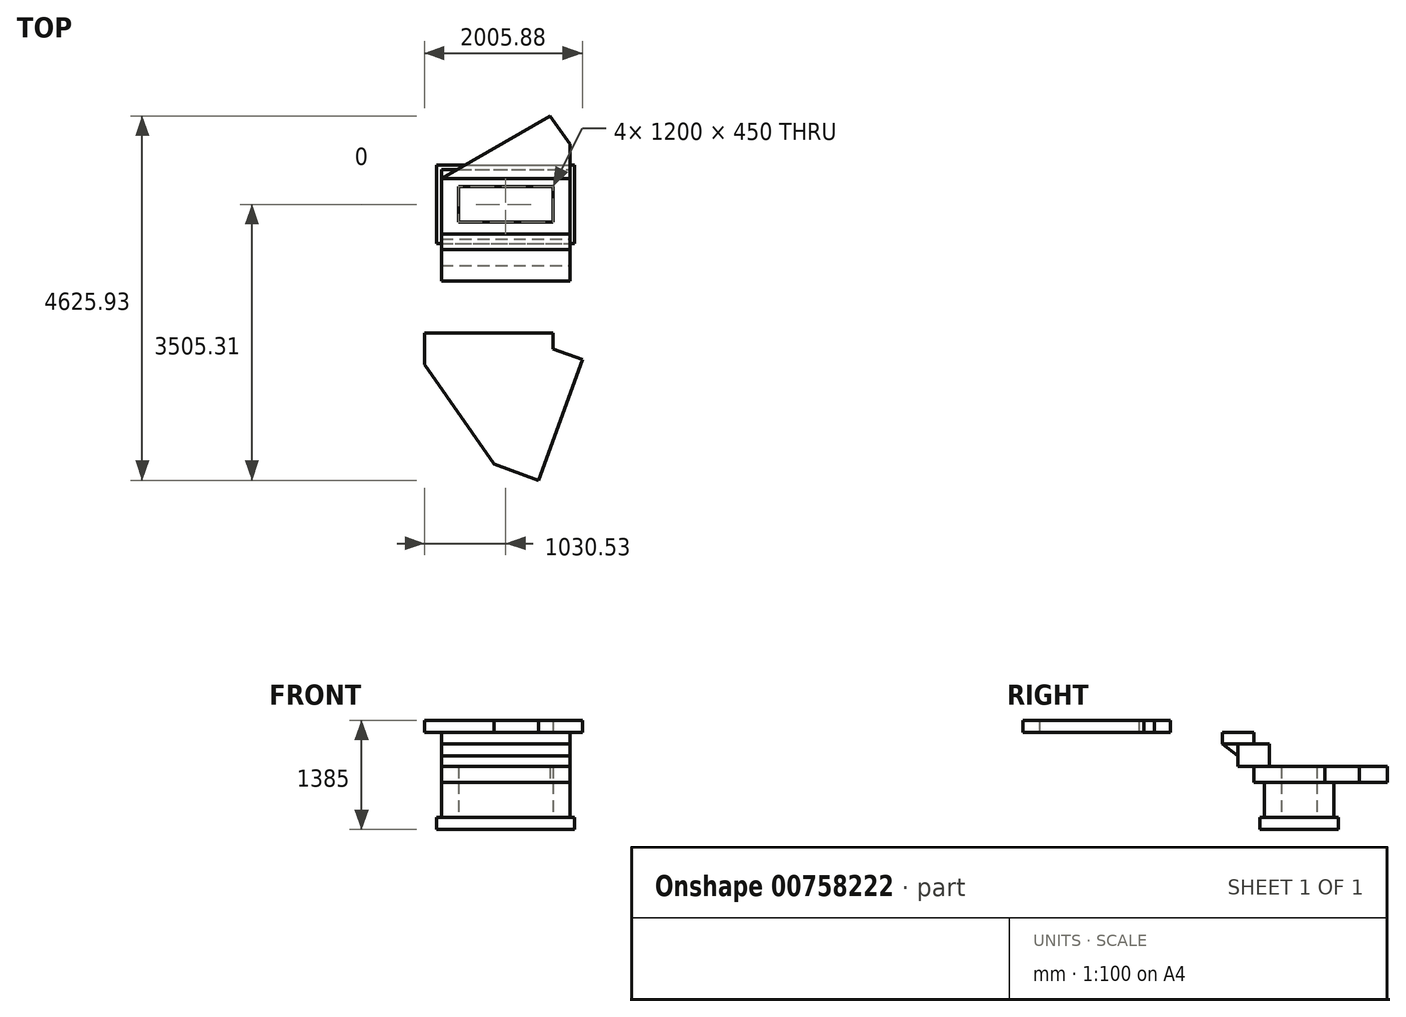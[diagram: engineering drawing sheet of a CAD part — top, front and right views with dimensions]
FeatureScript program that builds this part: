
annotation { "Feature Type Name" : "Feature", "Feature Type Description" : "" }
export const myFeature = defineFeature(function(context is Context, id is Id, definition is map)
    precondition{}
    {
        {
            var Q0;
            Q0=qCreatedBy(makeId("Top.planeOp"),FACE);
            var sketch = newSketch(context, id + "F0", { "sketchPlane" : qUnion([Q0])});
            skLineSegment(sketch, "E0", {"start": v(-102.22, -92.06) * mm, "end": v(-102.22, 907.94) * mm});
            skLineSegment(sketch, "E1", {"start": v(-102.22, 907.94) * mm, "end": v(1647.78, 907.94) * mm});
            skLineSegment(sketch, "E2", {"start": v(1647.78, 907.94) * mm, "end": v(1647.78, -92.06) * mm});
            skLineSegment(sketch, "E3", {"start": v(-102.22, -92.06) * mm, "end": v(1647.78, -92.06) * mm});
            skSolve(sketch);
        }
        {
            var Q0;
            Q0=makeQuery(id+"F0.imprint","IMPRINT",FACE,{"disambiguationData":[TD([[makeQuery(id+"F0.imprint","IMPRINT",EDGE,{"derivedFrom":sQuery(id+"F0.wireOp",EDGE,"E0")}),-1.0]])]});
            extrude(context, id + "F1", {"entities" : qUnion([Q0]), "depth" : 150 * mm, "offsetDistance" : 25 * mm});
        }
        {
            var Q0;
            Q0=makeQuery(id+"F1.opExtrude","CAP_FACE",FACE,{"disambiguationData":[OSD([sQuery(id+"F0.wireOp",EDGE,"E0"),sQuery(id+"F0.wireOp",EDGE,"E1"),sQuery(id+"F0.wireOp",EDGE,"E2"),sQuery(id+"F0.wireOp",EDGE,"E3")])],"isStart":false});
            var sketch = newSketch(context, id + "F2", { "sketchPlane" : qUnion([Q0])});
            skLineSegment(sketch, "E4.bottom", {"start": v(-42.22, -32.06) * mm, "end": v(1587.78, -32.06) * mm});
            skLineSegment(sketch, "E4.top", {"start": v(-42.22, 847.94) * mm, "end": v(1587.78, 847.94) * mm});
            skLineSegment(sketch, "E4.left", {"start": v(-42.22, -32.06) * mm, "end": v(-42.22, 847.94) * mm});
            skLineSegment(sketch, "E4.right", {"start": v(1587.78, -32.06) * mm, "end": v(1587.78, 847.94) * mm});
            skLineSegment(sketch, "E5.bottom", {"start": v(172.78, 182.94) * mm, "end": v(1372.78, 182.94) * mm});
            skLineSegment(sketch, "E5.top", {"start": v(172.78, 632.94) * mm, "end": v(1372.78, 632.94) * mm});
            skLineSegment(sketch, "E5.left", {"start": v(172.78, 182.94) * mm, "end": v(172.78, 632.94) * mm});
            skLineSegment(sketch, "E5.right", {"start": v(1372.78, 182.94) * mm, "end": v(1372.78, 632.94) * mm});
            skSolve(sketch);
        }
        {
            var Q0;
            Q0=makeQuery(id+"F2.imprint","IMPRINT",FACE,{"disambiguationData":[TD([[makeQuery(id+"F2.imprint","IMPRINT",EDGE,{"derivedFrom":sQuery(id+"F2.wireOp",EDGE,"E4.bottom")}),1.0]])]});
            extrude(context, id + "F3", {"entities" : qUnion([Q0]), "depth" : 450 * mm, "offsetDistance" : 25 * mm});
        }
        {
            var Q0;
            Q0=makeQuery(id+"F3.opExtrude","CAP_FACE",FACE,{"disambiguationData":[OSD([sQuery(id+"F2.wireOp",EDGE,"E4.bottom"),sQuery(id+"F2.wireOp",EDGE,"E4.top"),sQuery(id+"F2.wireOp",EDGE,"E4.left"),sQuery(id+"F2.wireOp",EDGE,"E4.right"),sQuery(id+"F2.wireOp",EDGE,"E5.bottom"),sQuery(id+"F2.wireOp",EDGE,"E5.top"),sQuery(id+"F2.wireOp",EDGE,"E5.left"),sQuery(id+"F2.wireOp",EDGE,"E5.right")])],"isStart":false});
            var sketch = newSketch(context, id + "F4", { "sketchPlane" : qUnion([Q0])});
            skLineSegment(sketch, "E6.bottom", {"start": v(172.78, 182.94) * mm, "end": v(1372.78, 182.94) * mm});
            skLineSegment(sketch, "E6.top", {"start": v(172.78, 632.94) * mm, "end": v(1372.78, 632.94) * mm});
            skLineSegment(sketch, "E6.left", {"start": v(172.78, 182.94) * mm, "end": v(172.78, 632.94) * mm});
            skLineSegment(sketch, "E6.right", {"start": v(1372.78, 182.94) * mm, "end": v(1372.78, 632.94) * mm});
            skLineSegment(sketch, "E7.bottom", {"start": v(-42.22, -167.06) * mm, "end": v(1587.78, -167.06) * mm});
            skLineSegment(sketch, "E7.top", {"start": v(-42.22, 732.94) * mm, "end": v(1587.78, 732.94) * mm});
            skLineSegment(sketch, "E7.left", {"start": v(-42.22, -167.06) * mm, "end": v(-42.22, 732.94) * mm});
            skLineSegment(sketch, "E7.right", {"start": v(1587.78, -167.06) * mm, "end": v(1587.78, 732.94) * mm});
            skSolve(sketch);
        }
        {
            var Q0;
            Q0=makeQuery(id+"F4.imprint","IMPRINT",FACE,{"disambiguationData":[TD([[makeQuery(id+"F4.imprint","IMPRINT",EDGE,{"derivedFrom":sQuery(id+"F4.wireOp",EDGE,"E7.bottom")}),1.0]])]});
            var Q1;
            Q1=makeQuery(id+"F4.imprint","IMPRINT",FACE,{"disambiguationData":[TD([[makeQuery(id+"F4.imprint","IMPRINT",EDGE,{"derivedFrom":sQuery(id+"F4.wireOp",EDGE,"E6.bottom")}),-1.0]])]});
            extrude(context, id + "F5", {"entities" : qUnion([Q0, Q1]), "depth" : 200 * mm, "offsetDistance" : 25 * mm});
        }
        {
            var Q0;
            Q0=makeQuery(id+"F5.opExtrude","CAP_FACE",FACE,{"disambiguationData":[OSD([sQuery(id+"F4.wireOp",EDGE,"E6.bottom"),sQuery(id+"F4.wireOp",EDGE,"E6.top"),sQuery(id+"F4.wireOp",EDGE,"E6.left"),sQuery(id+"F4.wireOp",EDGE,"E6.right"),sQuery(id+"F4.wireOp",EDGE,"E7.bottom"),sQuery(id+"F4.wireOp",EDGE,"E7.top"),sQuery(id+"F4.wireOp",EDGE,"E7.left"),sQuery(id+"F4.wireOp",EDGE,"E7.right")])],"isStart":false});
            var sketch = newSketch(context, id + "F6", { "sketchPlane" : qUnion([Q0])});
            skLineSegment(sketch, "E8.bottom", {"start": v(-42.22, 32.94) * mm, "end": v(1587.78, 32.94) * mm});
            skLineSegment(sketch, "E8.top", {"start": v(-42.22, -367.06) * mm, "end": v(1587.78, -367.06) * mm});
            skLineSegment(sketch, "E9", {"start": v(1587.78, 32.94) * mm, "end": v(1587.78, -367.06) * mm});
            skLineSegment(sketch, "E10", {"start": v(-42.22, 32.94) * mm, "end": v(-42.22, -367.06) * mm});
            skSolve(sketch);
        }
        {
            var Q0;
            {var subQ0=sQuery(id+"F6.wireOp",EDGE,"E8.top");Q0=makeQuery(id+"F6.imprint","IMPRINT",FACE,{"disambiguationData":[TD([[makeQuery(id+"F6.imprint","IMPRINT",EDGE,{"derivedFrom":subQ0}),1.0]])]});}
            var Q1;
            {var subQ0=sQuery(id+"F6.wireOp",EDGE,"E8.bottom");Q1=makeQuery(id+"F6.imprint","IMPRINT",FACE,{"disambiguationData":[TD([[makeQuery(id+"F6.imprint","IMPRINT",EDGE,{"derivedFrom":subQ0}),-1.0]])]});}
            extrude(context, id + "F7", {"entities" : qUnion([Q0, Q1]), "depth" : 285 * mm, "offsetDistance" : 25 * mm});
        }
        {
            var Q0;
            Q0=makeQuery(id+"F7.opExtrude","CAP_FACE",FACE,{"disambiguationData":[OSD([sQuery(id+"F6.wireOp",EDGE,"E8.bottom"),sQuery(id+"F6.wireOp",EDGE,"E8.top"),sQuery(id+"F6.wireOp",EDGE,"E8.left"),sQuery(id+"F6.wireOp",EDGE,"E8.right")])],"isStart":false});
            var sketch = newSketch(context, id + "F8", { "sketchPlane" : qUnion([Q0])});
            skLineSegment(sketch, "E11.right", {"start": v(-42.22, -167.06) * mm, "end": v(-42.22, -567.06) * mm});
            skLineSegment(sketch, "E12", {"start": v(-42.22, -567.06) * mm, "end": v(1587.78, -567.06) * mm});
            skLineSegment(sketch, "E13", {"start": v(1587.78, -567.06) * mm, "end": v(1587.78, -167.06) * mm});
            skLineSegment(sketch, "E14", {"start": v(1587.78, -167.06) * mm, "end": v(-42.22, -167.06) * mm});
            skSolve(sketch);
        }
        {
            var Q0;
            {var subQ2=sQuery(id+"F8.wireOp",EDGE,"E12");Q0=makeQuery(id+"F8.imprint","IMPRINT",FACE,{"disambiguationData":[TD([[makeQuery(id+"F8.imprint","IMPRINT",EDGE,{"derivedFrom":subQ2}),1.0]])]});}
            var Q1;
            {var subQ2=sQuery(id+"F8.wireOp",EDGE,"E14");Q1=makeQuery(id+"F8.imprint","IMPRINT",FACE,{"disambiguationData":[TD([[makeQuery(id+"F8.imprint","IMPRINT",EDGE,{"derivedFrom":subQ2}),1.0]])]});}
            extrude(context, id + "F9", {"entities" : qUnion([Q0, Q1]), "depth" : 150 * mm, "offsetDistance" : 25 * mm});
        }
        {
            var Q0;
            Q0=makeQuery(id+"F9.opExtrude","SWEPT_FACE",FACE,{"disambiguationData":[OSD([sQuery(id+"F8.wireOp",EDGE,"E13")])]});
            var sketch = newSketch(context, id + "F10", { "sketchPlane" : qUnion([Q0])});
            skLineSegment(sketch, "E15.0", {"start": v(-367.06, 1085) * mm, "end": v(-367.06, 935) * mm});
            skLineSegment(sketch, "E16.0", {"start": v(-567.06, 1085) * mm, "end": v(-367.06, 1085) * mm});
            skLineSegment(sketch, "E17", {"start": v(-567.06, 1085) * mm, "end": v(-367.06, 935) * mm});
            skPoint(sketch, "E18.orphan", {"position": v(-367.06, 800) * mm});
            skPoint(sketch, "E19.orphan", {"position": v(-167.06, 1085) * mm});
            skSolve(sketch);
        }
        {
            var Q0;
            Q0=makeQuery(id+"F10.imprint","IMPRINT",FACE,{"disambiguationData":[TD([[makeQuery(id+"F10.imprint","IMPRINT",EDGE,{"derivedFrom":sQuery(id+"F10.wireOp",EDGE,"E15.0")}),-1.0]])]});
            extrude(context, id + "F11", {"entities" : qUnion([Q0]), "oppositeDirection" : true, "depth" : 1630 * mm, "offsetDistance" : 25 * mm});
        }
        {
            var Q0;
            Q0=makeQuery(id+"F9.opExtrude","CAP_FACE",FACE,{"disambiguationData":[OSD([sQuery(id+"F8.wireOp",EDGE,"E11.right"),sQuery(id+"F8.wireOp",EDGE,"E12"),sQuery(id+"F8.wireOp",EDGE,"E13"),sQuery(id+"F8.wireOp",EDGE,"E14")])],"isStart":false});
            var sketch = newSketch(context, id + "F12", { "sketchPlane" : qUnion([Q0])});
            skLineSegment(sketch, "E20", {"start": v(129.99, -1001.66) * mm, "end": v(1759.99, -1001.66) * mm});
            skLineSegment(sketch, "E21", {"start": v(1759.99, -1001.66) * mm, "end": v(1759.99, -2831.66) * mm});
            skLineSegment(sketch, "E22", {"start": v(1759.99, -2831.66) * mm, "end": v(-70.01, -2831.66) * mm});
            skLineSegment(sketch, "E23", {"start": v(-70.01, -2831.66) * mm, "end": v(-70.01, -1201.66) * mm});
            skLineSegment(sketch, "E24", {"start": v(-70.01, -1201.66) * mm, "end": v(129.99, -1201.66) * mm});
            skLineSegment(sketch, "E25", {"start": v(129.99, -1201.66) * mm, "end": v(129.99, -1001.66) * mm});
            skSolve(sketch);
        }
        {
            var Q0;
            Q0=makeQuery(id+"F12.imprint","IMPRINT",FACE,{"disambiguationData":[TD([[makeQuery(id+"F12.imprint","IMPRINT",EDGE,{"derivedFrom":sQuery(id+"F12.wireOp",EDGE,"E20")}),-1.0]])]});
            extrude(context, id + "F13", {"entities" : qUnion([Q0]), "depth" : 150 * mm, "offsetDistance" : 25 * mm});
        }
        {
            var Q0;
            Q0=makeQuery(id+"F13.opExtrude","CAP_FACE",FACE,{"disambiguationData":[OSD([sQuery(id+"F12.wireOp",EDGE,"E20"),sQuery(id+"F12.wireOp",EDGE,"E21"),sQuery(id+"F12.wireOp",EDGE,"E22"),sQuery(id+"F12.wireOp",EDGE,"E23"),sQuery(id+"F12.wireOp",EDGE,"E24"),sQuery(id+"F12.wireOp",EDGE,"E25")])],"isStart":false});
            var sketch = newSketch(context, id + "F14", { "sketchPlane" : qUnion([Q0])});
            skLineSegment(sketch, "E26.bottom", {"start": v(-463.78, -1746.24) * mm, "end": v(-2078.78, -1746.24) * mm});
            skLineSegment(sketch, "E26.top", {"start": v(-463.78, -4791.24) * mm, "end": v(-2078.78, -4791.24) * mm});
            skLineSegment(sketch, "E26.left", {"start": v(-463.78, -1746.24) * mm, "end": v(-463.78, -4791.24) * mm});
            skLineSegment(sketch, "E26.right", {"start": v(-2078.78, -1746.24) * mm, "end": v(-2078.78, -4791.24) * mm});
            skSolve(sketch);
        }
        {
            var Q0;
            Q0=makeQuery(id+"F14.imprint","IMPRINT",FACE,{"disambiguationData":[TD([[makeQuery(id+"F14.imprint","IMPRINT",EDGE,{"derivedFrom":sQuery(id+"F14.wireOp",EDGE,"E26.bottom")}),1.0]])]});
            extrude(context, id + "F15", {"entities" : qUnion([Q0]), "depth" : 150 * mm, "offsetDistance" : 25 * mm});
        }
        {
            var Q0;
            Q0=makeQuery(id+"F13.opExtrude","SWEPT_BODY",BODY,{"disambiguationData":[OSD([sQuery(id+"F12.wireOp",EDGE,"E20"),sQuery(id+"F12.wireOp",EDGE,"E21"),sQuery(id+"F12.wireOp",EDGE,"E22"),sQuery(id+"F12.wireOp",EDGE,"E23"),sQuery(id+"F12.wireOp",EDGE,"E24"),sQuery(id+"F12.wireOp",EDGE,"E25")])]});
            deleteBodies(context, id + "F16", {"entities" : qUnion([Q0])});
        }
        {
            var Q0;
            Q0=makeQuery(id+"F15.opExtrude","SWEPT_BODY",BODY,{"disambiguationData":[OSD([sQuery(id+"F14.wireOp",EDGE,"E26.bottom"),sQuery(id+"F14.wireOp",EDGE,"E26.top"),sQuery(id+"F14.wireOp",EDGE,"E26.left"),sQuery(id+"F14.wireOp",EDGE,"E26.right")])]});
            deleteBodies(context, id + "F17", {"entities" : qUnion([Q0])});
        }
        {
            var Q0;
            Q0=makeQuery(id+"F3.opExtrude","CAP_FACE",FACE,{"disambiguationData":[OSD([sQuery(id+"F2.wireOp",EDGE,"E4.bottom"),sQuery(id+"F2.wireOp",EDGE,"E4.top"),sQuery(id+"F2.wireOp",EDGE,"E4.left"),sQuery(id+"F2.wireOp",EDGE,"E4.right"),sQuery(id+"F2.wireOp",EDGE,"E5.bottom"),sQuery(id+"F2.wireOp",EDGE,"E5.top"),sQuery(id+"F2.wireOp",EDGE,"E5.left"),sQuery(id+"F2.wireOp",EDGE,"E5.right")])],"isStart":false});
            var sketch = newSketch(context, id + "F18", { "sketchPlane" : qUnion([Q0])});
            skPoint(sketch, "E27.0", {"position": v(1587.78, 732.94) * mm});
            skPoint(sketch, "E28.0", {"position": v(-42.22, 732.94) * mm});
            skLineSegment(sketch, "E29", {"start": v(1587.78, 732.94) * mm, "end": v(-42.22, 732.94) * mm});
            skLineSegment(sketch, "E30", {"start": v(1587.78, 732.94) * mm, "end": v(1587.78, 1170.64) * mm});
            skLineSegment(sketch, "E31", {"start": v(1587.78, 1170.64) * mm, "end": v(1335.83, 1528.56) * mm});
            skLineSegment(sketch, "E32", {"start": v(1335.83, 1528.56) * mm, "end": v(-42.22, 732.94) * mm});
            skSolve(sketch);
        }
        {
            var Q0;
            {var subQ3=sQuery(id+"F18.wireOp",EDGE,"E31");Q0=makeQuery(id+"F18.imprint","IMPRINT",FACE,{"disambiguationData":[TD([[makeQuery(id+"F18.imprint","IMPRINT",EDGE,{"derivedFrom":subQ3}),1.0]])]});}
            var Q1;
            {var subQ0=sQuery(id+"F18.wireOp",EDGE,"E29");Q1=makeQuery(id+"F18.imprint","IMPRINT",FACE,{"disambiguationData":[TD([[makeQuery(id+"F18.imprint","IMPRINT",EDGE,{"derivedFrom":subQ0}),-1.0]])]});}
            extrude(context, id + "F19", {"entities" : qUnion([Q0, Q1]), "depth" : 200 * mm, "offsetDistance" : 25 * mm});
        }
        {
            var Q0;
            Q0=makeQuery(id+"F9.opExtrude","CAP_FACE",FACE,{"disambiguationData":[OSD([sQuery(id+"F8.wireOp",EDGE,"E11.right"),sQuery(id+"F8.wireOp",EDGE,"E12"),sQuery(id+"F8.wireOp",EDGE,"E13"),sQuery(id+"F8.wireOp",EDGE,"E14")])],"isStart":false});
            var sketch = newSketch(context, id + "F20", { "sketchPlane" : qUnion([Q0])});
            skLineSegment(sketch, "E33", {"start": v(1372.25, -1228.87) * mm, "end": v(-257.75, -1228.87) * mm});
            skLineSegment(sketch, "E34", {"start": v(1372.25, -1228.87) * mm, "end": v(1372.25, -1428.87) * mm});
            skLineSegment(sketch, "E35", {"start": v(1372.25, -1428.87) * mm, "end": v(1748.13, -1565.68) * mm});
            skLineSegment(sketch, "E36", {"start": v(1748.13, -1565.68) * mm, "end": v(1190.64, -3097.37) * mm});
            skLineSegment(sketch, "E37", {"start": v(1190.64, -3097.37) * mm, "end": v(626.82, -2892.16) * mm});
            skLineSegment(sketch, "E38", {"start": v(-257.75, -1228.87) * mm, "end": v(-257.75, -1628.87) * mm});
            skLineSegment(sketch, "E39", {"start": v(-257.75, -1628.87) * mm, "end": v(626.82, -2892.16) * mm});
            skSolve(sketch);
        }
        {
            var Q0;
            Q0=makeQuery(id+"F20.imprint","IMPRINT",FACE,{"disambiguationData":[TD([[makeQuery(id+"F20.imprint","IMPRINT",EDGE,{"derivedFrom":sQuery(id+"F20.wireOp",EDGE,"E33")}),1.0]])]});
            extrude(context, id + "F21", {"entities" : qUnion([Q0]), "depth" : 150 * mm, "offsetDistance" : 25 * mm});
        }
    });
